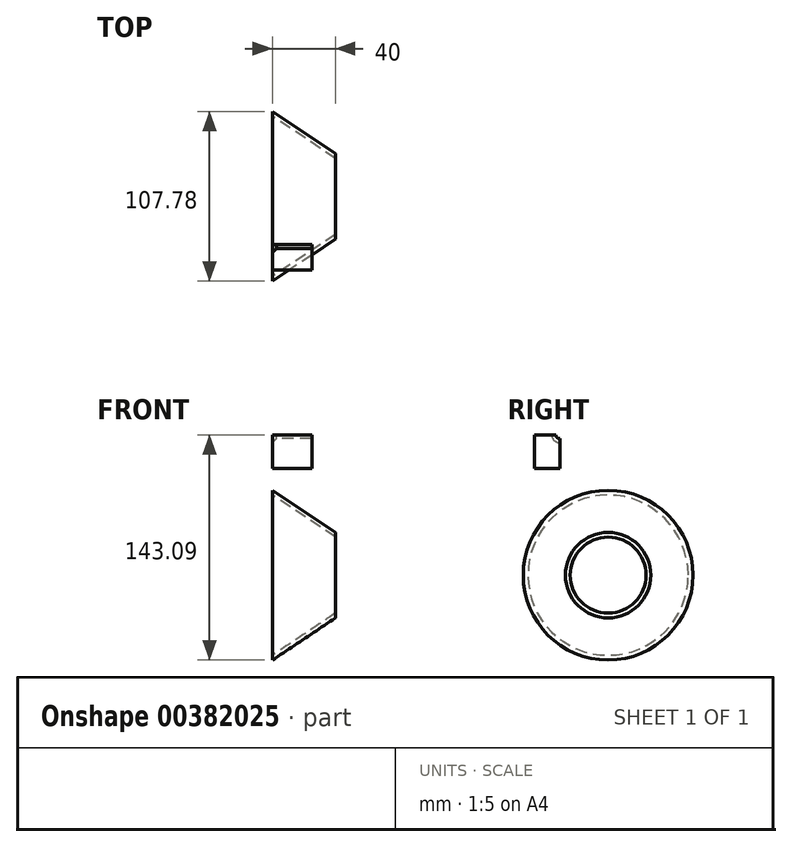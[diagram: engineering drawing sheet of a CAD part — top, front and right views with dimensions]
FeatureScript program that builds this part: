
annotation { "Feature Type Name" : "Feature", "Feature Type Description" : "" }
export const myFeature = defineFeature(function(context is Context, id is Id, definition is map)
    precondition{}
    {
        {
            var Q0;
            Q0=qCreatedBy(makeId("Right.planeOp"),FACE);
            var sketch = newSketch(context, id + "F0", { "sketchPlane" : qUnion([Q0])});
            skCircle(sketch, "E0", {"center": v(0, 0) * mm, "radius": 53.9 * mm});
            skSolve(sketch);
        }
        {
            var Q0;
            Q0=qCreatedBy(makeId("Right.planeOp"),FACE);
            cPlane(context, id + "F1", {"entities" : qUnion([Q0]), "cplaneType" : CPlaneType.OFFSET, "offset" : 40 * mm, "width" : 150 * mm, "height" : 150 * mm});
        }
        {
            var Q0;
            Q0=qCreatedBy(id+"F1.planeOp",FACE);
            var sketch = newSketch(context, id + "F2", { "sketchPlane" : qUnion([Q0])});
            skCircle(sketch, "E1", {"center": v(0, 0) * mm, "radius": 27.14 * mm});
            skSolve(sketch);
        }
        {
            var Q0;
            Q0 = qSketchRegion(id + "F0", true);
            var Q1;
            Q1=makeQuery(id+"F2.imprint","IMPRINT",FACE,{"disambiguationData":[TD([[makeQuery(id+"F2.imprint","IMPRINT",EDGE,{"derivedFrom":sQuery(id+"F2.wireOp",EDGE,"E1")}),1.0]])]});
            loft(context, id + "F3", {"sheetProfilesArray" : [{ "sheetProfileEntities" : qUnion([Q0]) }, { "sheetProfileEntities" : qUnion([Q1]) }]});
        }
        {
            var Q0;
            Q0=makeQuery(id+"F3.opLoft","CAP_FACE",FACE,{"disambiguationData":[OSD([makeQuery(id+"F2.imprint","IMPRINT",FACE,{"disambiguationData":[TD([[makeQuery(id+"F2.imprint","IMPRINT",EDGE,{"derivedFrom":sQuery(id+"F2.wireOp",EDGE,"E1")}),1.0]])]})])],"isStart":true});
            var Q1;
            Q1=makeQuery(id+"F3.opLoft","CAP_FACE",FACE,{"disambiguationData":[OSD([makeQuery(id+"F0.imprint","IMPRINT",FACE,{"disambiguationData":[TD([[makeQuery(id+"F0.imprint","IMPRINT",EDGE,{"derivedFrom":sQuery(id+"F0.wireOp",EDGE,"E0")}),1.0]])]})])],"isStart":true});
            shell(context, id + "F4", {"entities" : qUnion([Q0, Q1]), "thickness" : 2.5 * mm});
        }
        {
            var Q0;
            Q0=qCreatedBy(makeId("Right.planeOp"),FACE);
            var sketch = newSketch(context, id + "F5", { "sketchPlane" : qUnion([Q0])});
            skLineSegment(sketch, "E2.bottom", {"start": v(-30.73, 89.2) * mm, "end": v(-46.85, 89.2) * mm});
            skLineSegment(sketch, "E2.top", {"start": v(-30.73, 67.7) * mm, "end": v(-46.85, 67.7) * mm});
            skLineSegment(sketch, "E2.left", {"start": v(-30.73, 89.2) * mm, "end": v(-30.73, 67.7) * mm});
            skLineSegment(sketch, "E2.right", {"start": v(-46.85, 89.2) * mm, "end": v(-46.85, 67.7) * mm});
            skSolve(sketch);
        }
        {
            var Q0;
            Q0 = qSketchRegion(id + "F5", true);
            extrude(context, id + "F6", {"entities" : qUnion([Q0]), "depth" : 25 * mm});
        }
        {
            var Q0;
            Q0=sQuery(id+"F5.wireOp",VERTEX,"E2.left.start");
            var Q1;
            Q1=makeQuery(id+"F6.opExtrude","SWEPT_BODY",BODY,{"disambiguationData":[OSD([sQuery(id+"F5.wireOp",EDGE,"E2.bottom"),sQuery(id+"F5.wireOp",EDGE,"E2.top"),sQuery(id+"F5.wireOp",EDGE,"E2.left"),sQuery(id+"F5.wireOp",EDGE,"E2.right")])]});
            hole(context, id + "F7", {"style" : HoleStyle.C_SINK, "endStyle" : HoleEndStyle.THROUGH, "oppositeDirection" : true, "holeDiameter" : 5 * mm, "cSinkDiameter" : 10 * mm, "cSinkAngle" : 90 * degree, "isTappedThrough" : true, "tappedDepth" : 12 * mm, "tapClearance" : 3, "startFromSketch" : true, "locations" : qUnion([Q0]), "scope" : qUnion([Q1])});
        }
    });
